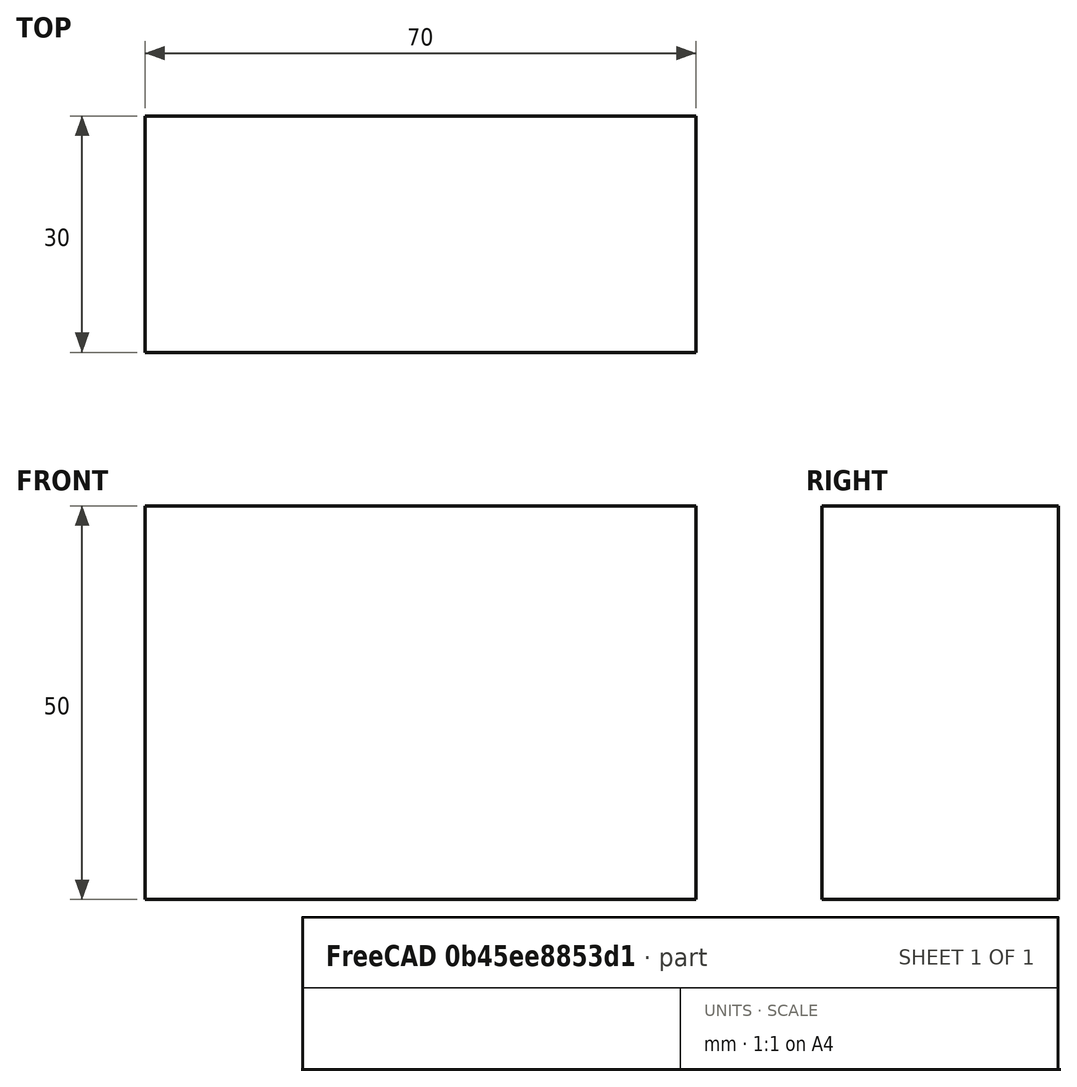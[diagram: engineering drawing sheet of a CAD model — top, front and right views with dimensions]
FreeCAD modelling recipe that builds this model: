
FCSTD DOCUMENT  (FreeCAD 0.15R4671 (Git))
Label: Flat Bar 70x30 EN10058 S235JR
License: All rights reserved
LicenseURL: http://en.wikipedia.org/wiki/All_rights_reserved
objects: Sketcher::SketchObject×1, Part::Extrusion×1
note: 2 computed .brp shape members not serialized (recipe doc carries the construction recipe); baked Part::Feature solids carry a one-line shape summary decoded from their .brp

FEATURE [Sketcher::SketchObject] Sketch
  sketch-geometry (4):
    g0: LineSegment StartX=-35 StartY=-15 StartZ=0 EndX=35 EndY=-15 EndZ=0
    g1: LineSegment StartX=35 StartY=-15 StartZ=0 EndX=35 EndY=15 EndZ=0
    g2: LineSegment StartX=35 StartY=15 StartZ=0 EndX=-35 EndY=15 EndZ=0
    g3: LineSegment StartX=-35 StartY=15 StartZ=0 EndX=-35 EndY=-15 EndZ=0
  constraints (12):
    c: Coincident(g0,g1)
    c: Coincident(g1,g2)
    c: Coincident(g2,g3)
    c: Coincident(g3,g0)
    c: Horizontal(g0)
    c: Horizontal(g2)
    c: Vertical(g1)
    c: Vertical(g3)
    c: Symmetric(g1,g2,g-2)
    c: Symmetric(g0,g1,g-1)
    c: DistanceY(g1) = 30
    c: DistanceX(g0) = 70
FEATURE [Part::Extrusion] Extrude  label="Flat Bar 70x30 EN10058 S235JR"
  Base = -> Sketch
  Dir = (0,0,50)
  Solid = true
